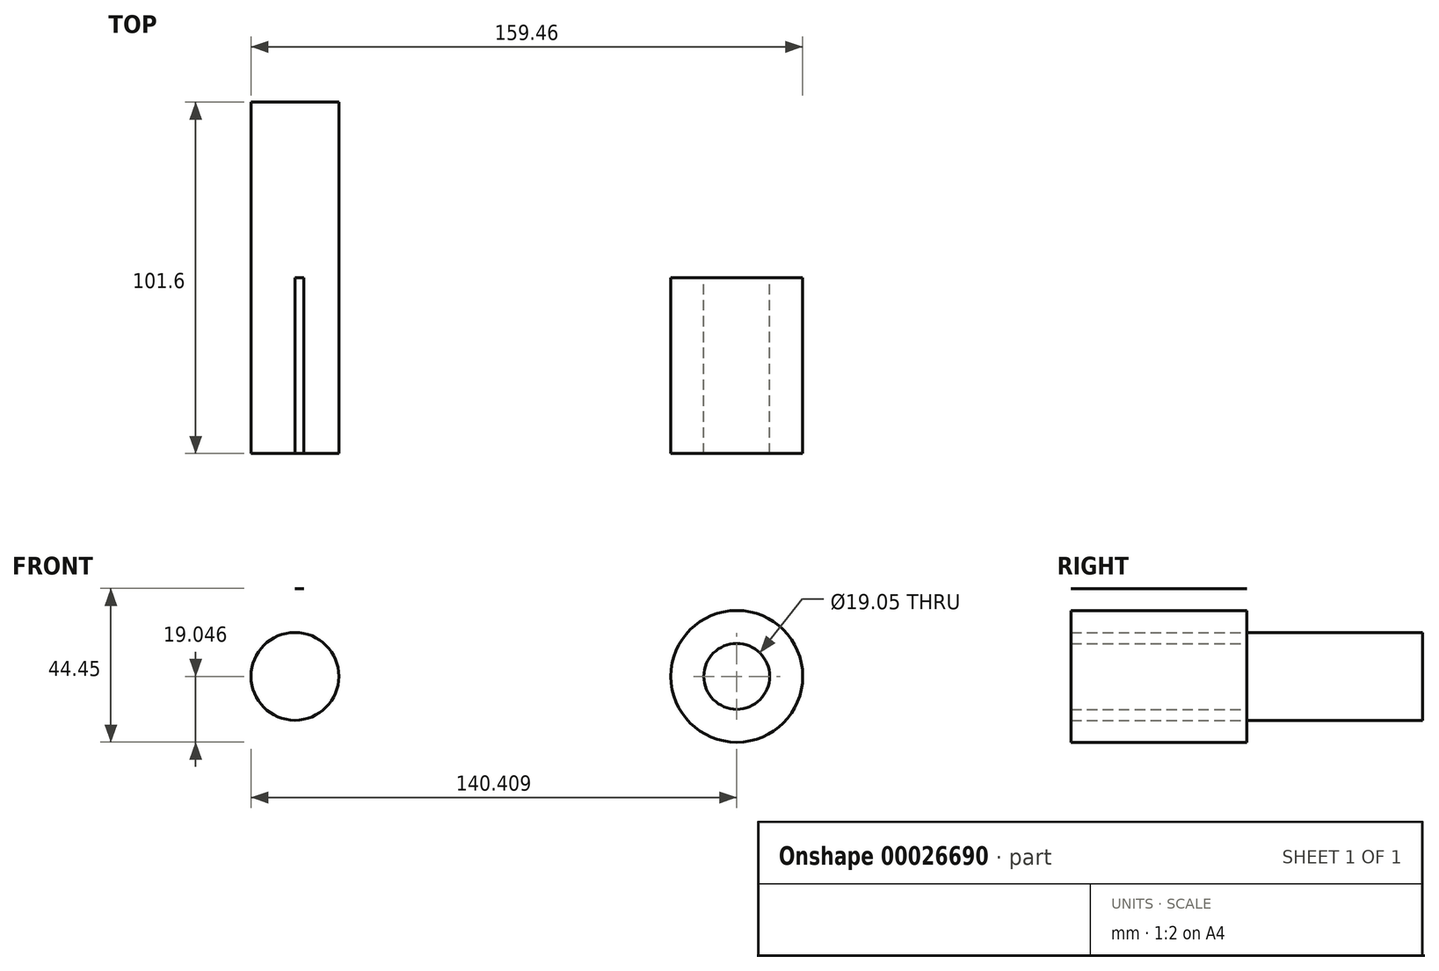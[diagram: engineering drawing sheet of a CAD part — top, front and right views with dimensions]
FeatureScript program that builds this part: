
annotation { "Feature Type Name" : "Feature", "Feature Type Description" : "" }
export const myFeature = defineFeature(function(context is Context, id is Id, definition is map)
    precondition{}
    {
        {
            var Q0;
            Q0=qCreatedBy(makeId("Front.planeOp"),FACE);
            var sketch = newSketch(context, id + "F0", { "sketchPlane" : qUnion([Q0])});
            skCircle(sketch, "E0", {"center": v(-113.8, 16.2) * mm, "radius": 25.4 * mm});
            skCircle(sketch, "E1", {"center": v(13.92, 16.2) * mm, "radius": 19.05 * mm});
            skLineSegment(sketch, "E2", {"start": v(-113.8, 41.6) * mm, "end": v(13.92, 35.26) * mm});
            skLineSegment(sketch, "E3", {"start": v(-113.8, -9.2) * mm, "end": v(13.92, -2.84) * mm});
            skCircle(sketch, "E4", {"center": v(-113.8, 16.2) * mm, "radius": 12.7 * mm});
            skCircle(sketch, "E5", {"center": v(13.92, 16.2) * mm, "radius": 9.53 * mm});
            skSolve(sketch);
        }
        {
            var Q0;
            {var subQ1=sQuery(id+"F0.wireOp",EDGE,"E0");var subQ5=sQuery(id+"F0.wireOp",EDGE,"E2");var subQ6=makeQuery(id+"F0.imprint","INTERSECT",VERTEX,{"disambiguationData":[OD(1.0)],"derivedFrom":[subQ1,subQ5]});Q0=makeQuery(id+"F0.imprint","IMPRINT",FACE,{"disambiguationData":[TD([[makeQuery(id+"F0.imprint","IMPRINT",EDGE,{"disambiguationData":[TD([[subQ6,1.0]])],"derivedFrom":subQ1}),-1.0]])]});}
            var Q1;
            {var subQ1=sQuery(id+"F0.wireOp",EDGE,"E0");var subQ4=sQuery(id+"F0.wireOp",EDGE,"E2");var subQ6=makeQuery(id+"F0.imprint","INTERSECT",VERTEX,{"disambiguationData":[OD(0.0)],"derivedFrom":[subQ1,subQ4]});Q1=makeQuery(id+"F0.imprint","IMPRINT",FACE,{"disambiguationData":[TD([[makeQuery(id+"F0.imprint","IMPRINT",EDGE,{"disambiguationData":[TD([[subQ6,-1.0]])],"derivedFrom":subQ1}),1.0]])]});}
            var Q2;
            {var subQ0=sQuery(id+"F0.wireOp",EDGE,"E1");var subQ2=makeQuery(id+"F0.imprint","INTERSECT",VERTEX,{"derivedFrom":[subQ0,sQuery(id+"F0.wireOp",EDGE,"E2")]});Q2=makeQuery(id+"F0.imprint","IMPRINT",FACE,{"disambiguationData":[TD([[makeQuery(id+"F0.imprint","IMPRINT",EDGE,{"disambiguationData":[TD([[subQ2,-1.0]])],"derivedFrom":subQ0}),1.0]])]});}
            extrude(context, id + "F1", {"entities" : qUnion([Q0, Q1, Q2]), "depth" : 50.8 * mm});
        }
        {
            var Q0;
            Q0=makeQuery(id+"F0.imprint","IMPRINT",FACE,{"disambiguationData":[TD([[makeQuery(id+"F0.imprint","IMPRINT",EDGE,{"derivedFrom":sQuery(id+"F0.wireOp",EDGE,"E4")}),1.0]])]});
            extrude(context, id + "F2", {"entities" : qUnion([Q0]), "operationType" : NewBodyOperationType.ADD, "depth" : 50.8 * mm});
        }
        {
            var Q0;
            Q0=makeQuery(id+"F0.imprint","IMPRINT",FACE,{"disambiguationData":[TD([[makeQuery(id+"F0.imprint","IMPRINT",EDGE,{"derivedFrom":sQuery(id+"F0.wireOp",EDGE,"E4")}),1.0]])]});
            extrude(context, id + "F3", {"entities" : qUnion([Q0]), "operationType" : NewBodyOperationType.ADD, "oppositeDirection" : true, "depth" : 50.8 * mm});
        }
    });
